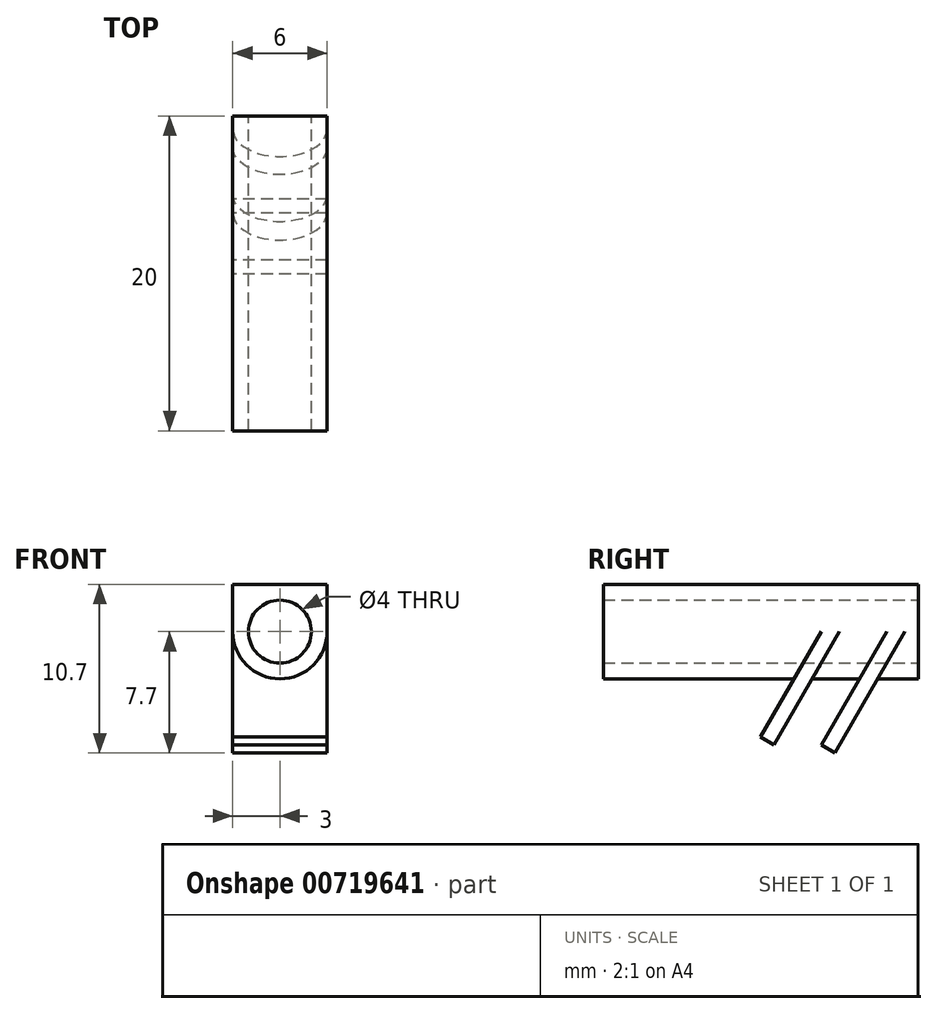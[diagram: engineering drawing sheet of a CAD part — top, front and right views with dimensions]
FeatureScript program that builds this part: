
annotation { "Feature Type Name" : "Feature", "Feature Type Description" : "" }
export const myFeature = defineFeature(function(context is Context, id is Id, definition is map)
    precondition{}
    {
        {
            var Q0;
            Q0=qCreatedBy(makeId("Front.planeOp"),FACE);
            var sketch = newSketch(context, id + "F0", { "sketchPlane" : qUnion([Q0])});
            skCircle(sketch, "E0", {"center": v(0, 0) * mm, "radius": 2 * mm});
            skCircle(sketch, "E1", {"center": v(0, 0) * mm, "radius": 3 * mm});
            skLineSegment(sketch, "E2", {"start": v(3, 0) * mm, "end": v(3, 3) * mm});
            skLineSegment(sketch, "E3", {"start": v(3, 3) * mm, "end": v(0, 3) * mm});
            skLineSegment(sketch, "E4", {"start": v(0, 3) * mm, "end": v(-3, 3) * mm});
            skLineSegment(sketch, "E5", {"start": v(-3, 3) * mm, "end": v(-3, 0) * mm});
            skSolve(sketch);
        }
        {
            var Q0;
            Q0=makeQuery(id+"F0.imprint","IMPRINT",FACE,{"disambiguationData":[TD([[makeQuery(id+"F0.imprint","IMPRINT",EDGE,{"derivedFrom":sQuery(id+"F0.wireOp",EDGE,"E0")}),-1.0]])]});
            extrude(context, id + "F1", {"entities" : qUnion([Q0]), "depth" : 20 * mm, "offsetDistance" : 25 * mm});
        }
        {
            var Q0;
            Q0=qCreatedBy(makeId("Right.planeOp"),FACE);
            var sketch = newSketch(context, id + "F2", { "sketchPlane" : qUnion([Q0])});
            skLineSegment(sketch, "E6", {"start": v(0, 0) * mm, "end": v(0, -2) * mm});
            skLineSegment(sketch, "E7", {"start": v(0, -2) * mm, "end": v(-3.15, -2) * mm});
            skLineSegment(sketch, "E8", {"start": v(-3.15, -2) * mm, "end": v(-6.15, -7.2) * mm});
            skLineSegment(sketch, "E9", {"start": v(-6.15, -7.2) * mm, "end": v(-5.29, -7.7) * mm});
            skLineSegment(sketch, "E10", {"start": v(-5.29, -7.7) * mm, "end": v(-2, -2) * mm});
            skLineSegment(sketch, "E11", {"start": v(-3.15, -2) * mm, "end": v(-6.15, -2) * mm});
            skLineSegment(sketch, "E12", {"start": v(-6.15, -2) * mm, "end": v(-9.15, -7.2) * mm});
            skLineSegment(sketch, "E13", {"start": v(-9.15, -7.2) * mm, "end": v(-10.02, -6.7) * mm});
            skLineSegment(sketch, "E14", {"start": v(-10.02, -6.7) * mm, "end": v(-7.3, -2) * mm});
            skLineSegment(sketch, "E15", {"start": v(-7.3, -2) * mm, "end": v(-6.15, -2) * mm});
            skSolve(sketch);
        }
        {
            var Q0;
            {var subQ0=sQuery(id+"F2.wireOp",EDGE,"E8");Q0=makeQuery(id+"F2.imprint","IMPRINT",FACE,{"disambiguationData":[TD([[makeQuery(id+"F2.imprint","IMPRINT",EDGE,{"derivedFrom":subQ0}),1.0]])]});}
            var Q1;
            Q1=makeQuery(id+"F2.imprint","IMPRINT",FACE,{"disambiguationData":[TD([[makeQuery(id+"F2.imprint","IMPRINT",EDGE,{"derivedFrom":sQuery(id+"F2.wireOp",EDGE,"E12")}),-1.0]])]});
            extrude(context, id + "F3", {"entities" : qUnion([Q0, Q1]), "operationType" : NewBodyOperationType.ADD, "depth" : 3 * mm, "offsetDistance" : 25 * mm, "hasSecondDirection" : true, "secondDirectionOppositeDirection" : true, "secondDirectionDepth" : 3 * mm});
        }
        {
            var Q0;
            Q0=makeQuery(id+"F3.opExtrude","SWEPT_FACE",FACE,{"disambiguationData":[OSD([sQuery(id+"F2.wireOp",EDGE,"E10")])]});
            cPlane(context, id + "F4", {"entities" : qUnion([Q0]), "cplaneType" : CPlaneType.OFFSET, "offset" : 0 * mm, "width" : 150 * mm, "height" : 150 * mm});
        }
        {
            var Q0;
            Q0=qCreatedBy(id+"F4.planeOp",FACE);
            var sketch = newSketch(context, id + "F5", { "sketchPlane" : qUnion([Q0])});
            skLineSegment(sketch, "E16", {"start": v(3, 0) * mm, "end": v(3, -4) * mm});
            skLineSegment(sketch, "E17", {"start": v(3, -4) * mm, "end": v(1.5, -4) * mm});
            skLineSegment(sketch, "E18", {"start": v(1.5, -4) * mm, "end": v(3, 0) * mm});
            skLineSegment(sketch, "E19.MirrorCS", {"start": v(-3, 0) * mm, "end": v(-3, -4) * mm});
            skLineSegment(sketch, "E20.MirrorCS", {"start": v(-3, -4) * mm, "end": v(-1.5, -4) * mm});
            skLineSegment(sketch, "E21.MirrorCS", {"start": v(-1.5, -4) * mm, "end": v(-3, 0) * mm});
            skSolve(sketch);
        }
        {
            var Q0;
            Q0 = qSketchRegion(id + "F5", true);
            extrude(context, id + "F6", {"entities" : qUnion([Q0]), "operationType" : NewBodyOperationType.ADD, "oppositeDirection" : true, "depth" : 1 * mm, "offsetDistance" : 25 * mm});
        }
        {
            var Q0;
            Q0=makeQuery(id+"F3.opExtrude","SWEPT_FACE",FACE,{"disambiguationData":[OSD([sQuery(id+"F2.wireOp",EDGE,"E12")])]});
            cPlane(context, id + "F7", {"entities" : qUnion([Q0]), "cplaneType" : CPlaneType.OFFSET, "offset" : 0 * mm, "width" : 150 * mm, "height" : 150 * mm});
        }
        {
            var Q0;
            Q0=qCreatedBy(id+"F7.planeOp",FACE);
            var sketch = newSketch(context, id + "F8", { "sketchPlane" : qUnion([Q0])});
            skLineSegment(sketch, "E22", {"start": v(3, -2.5) * mm, "end": v(3, -6) * mm});
            skLineSegment(sketch, "E23", {"start": v(3, -6) * mm, "end": v(1.5, -6) * mm});
            skLineSegment(sketch, "E24", {"start": v(1.5, -6) * mm, "end": v(3, -2.5) * mm});
            skLineSegment(sketch, "E25.MirrorCS", {"start": v(-1.5, -6) * mm, "end": v(-3, -2.5) * mm});
            skLineSegment(sketch, "E26.MirrorCS", {"start": v(-3, -2.5) * mm, "end": v(-3, -6) * mm});
            skLineSegment(sketch, "E27.MirrorCS", {"start": v(-3, -6) * mm, "end": v(-1.5, -6) * mm});
            skSolve(sketch);
        }
        {
            var Q0;
            Q0 = qSketchRegion(id + "F8", true);
            extrude(context, id + "F9", {"entities" : qUnion([Q0]), "operationType" : NewBodyOperationType.ADD, "oppositeDirection" : true, "depth" : 1 * mm, "offsetDistance" : 25 * mm});
        }
        {
            var Q0;
            Q0 = qSketchRegion(id + "F0", true);
            extrude(context, id + "F10", {"entities" : qUnion([Q0]), "operationType" : NewBodyOperationType.ADD, "depth" : 20 * mm, "offsetDistance" : 25 * mm});
        }
    });
